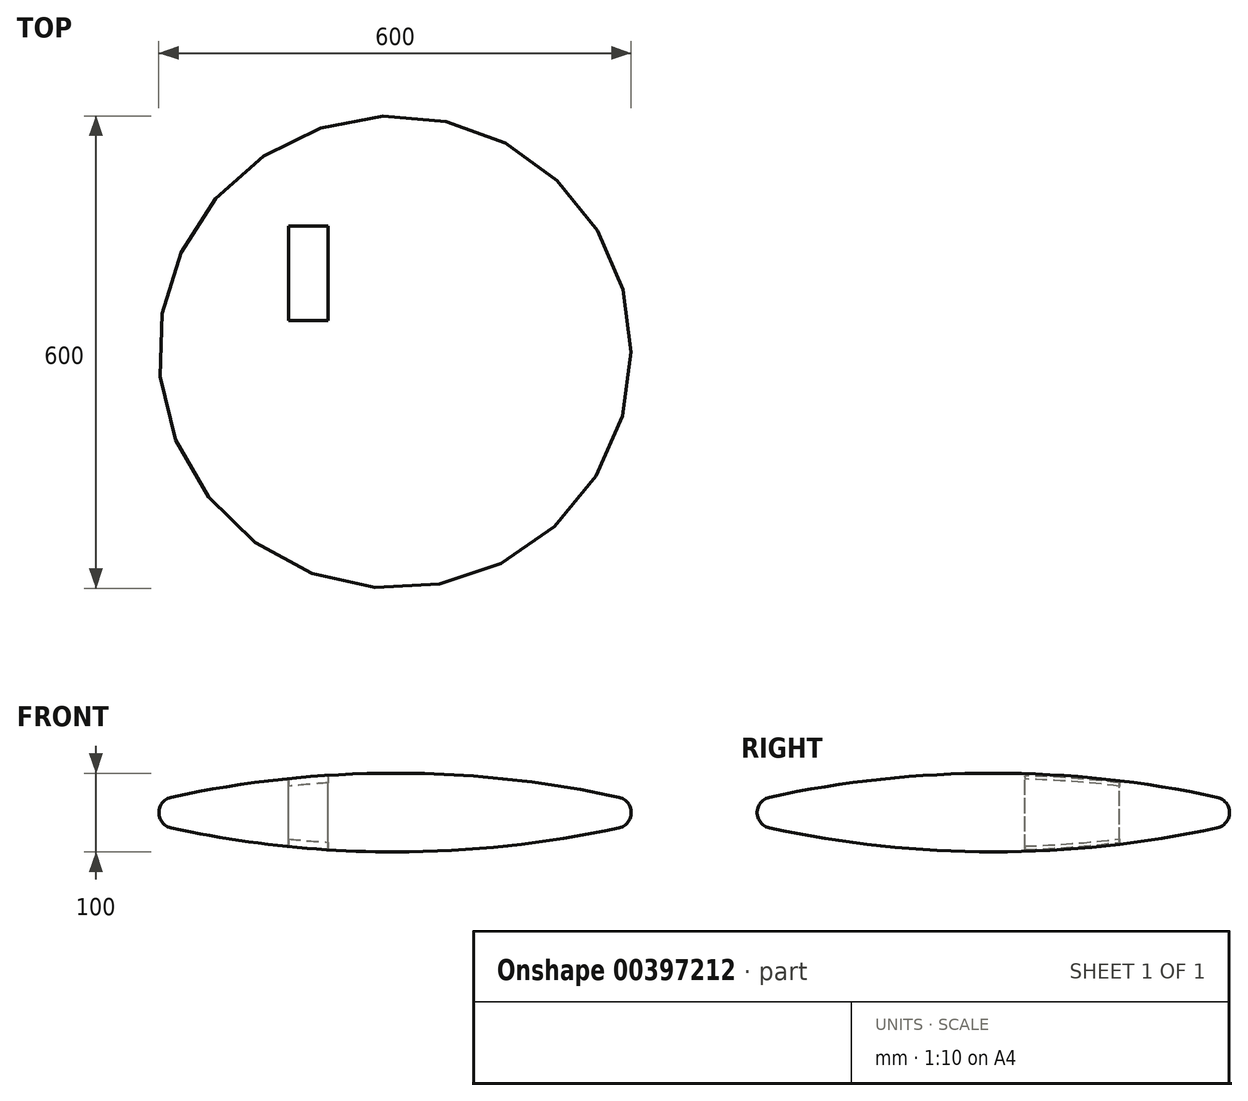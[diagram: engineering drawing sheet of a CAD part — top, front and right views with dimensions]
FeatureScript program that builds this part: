
annotation { "Feature Type Name" : "Feature", "Feature Type Description" : "" }
export const myFeature = defineFeature(function(context is Context, id is Id, definition is map)
    precondition{}
    {
        {
            var Q0;
            Q0=qCreatedBy(makeId("Front.planeOp"),FACE);
            var sketch = newSketch(context, id + "F0", { "sketchPlane" : qUnion([Q0])});
            skArc(sketch, "E0", {"start": v(284.24, 19.55) * mm, "mid": v(142.93, 42.36) * mm, "end": v(0, 50) * mm});
            skArc(sketch, "E1", {"start": v(284.24, -19.55) * mm, "mid": v(300, 0) * mm, "end": v(284.24, 19.55) * mm});
            skArc(sketch, "E2", {"start": v(0, -50) * mm, "mid": v(142.93, -42.36) * mm, "end": v(284.24, -19.55) * mm});
            skLineSegment(sketch, "E3", {"start": v(0, 50) * mm, "end": v(0, -50) * mm});
            skSolve(sketch);
        }
        {
            var Q0;
            Q0=makeQuery(id+"F0.imprint","IMPRINT",FACE,{"disambiguationData":[TD([[makeQuery(id+"F0.imprint","IMPRINT",EDGE,{"derivedFrom":sQuery(id+"F0.wireOp",EDGE,"E0")}),1.0]])]});
            var Q1;
            Q1=sQuery(id+"F0.wireOp",EDGE,"E3");
            revolve(context, id + "F1", {"entities" : qUnion([Q0]), "axis" : qUnion([Q1]), "revolveType" : RevolveType.FULL});
        }
        {
            var Q0;
            Q0=qCreatedBy(makeId("Top.planeOp"),FACE);
            var sketch = newSketch(context, id + "F2", { "sketchPlane" : qUnion([Q0])});
            skLineSegment(sketch, "E4.bottom", {"start": v(-135, 160) * mm, "end": v(-85, 160) * mm});
            skLineSegment(sketch, "E4.top", {"start": v(-135, 40) * mm, "end": v(-85, 40) * mm});
            skLineSegment(sketch, "E4.left", {"start": v(-135, 160) * mm, "end": v(-135, 40) * mm});
            skLineSegment(sketch, "E4.right", {"start": v(-85, 160) * mm, "end": v(-85, 40) * mm});
            skSolve(sketch);
        }
        {
            var Q0;
            Q0 = qSketchRegion(id + "F2", true);
            extrude(context, id + "F3", {"entities" : qUnion([Q0]), "operationType" : NewBodyOperationType.REMOVE, "endBound" : BoundingType.THROUGH_ALL, "oppositeDirection" : true, "depth" : 25 * mm, "hasSecondDirection" : true, "secondDirectionBound" : SecondDirectionBoundingType.THROUGH_ALL, "secondDirectionOppositeDirection" : false, "secondDirectionDepth" : 25 * mm});
        }
    });
